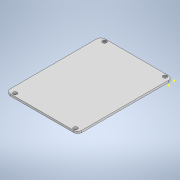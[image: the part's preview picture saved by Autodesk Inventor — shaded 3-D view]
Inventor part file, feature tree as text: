
AUTODESK INVENTOR PART (.ipt)
format: ipt  version: 2022 (Build 260153000, 153)  size: 626,176 bytes
history: native  units: mm
features: extrude x29, sketch x29, projected_geometry x11
ambient origin geometry x8: Origin, YZ Plane, XZ Plane, XY Plane, X Axis, Y Axis, Z Axis, Center Point
bodies: Body1 (feature_tree)
feature tree (69):
  extrude  "Extrusion8"  Depth=3.0mm TaperAngle=0.0deg
  extrude  "Extrusion9"  Depth=71.5mm
  extrude  "Extrusion10"  Depth=8.0mm
  extrude  "Extrusion11"  Depth=8.0mm
  extrude  "Extrusion12"  Depth=6.0mm
  extrude  "Extrusion13"  Depth=8.14mm
  extrude  "Extrusion14"  Depth=7.1mm
  sketch  "Sketch19"  dims[d82=6.0mm d83=7.1mm]
  extrude  "Extrusion16"  Depth=7.0mm
  extrude  "Extrusion17"  Depth=2.5mm
  extrude  "Extrusion18"  Depth=1.0mm
  extrude  "Extrusion19"  Depth=1.5mm
  extrude  "Extrusion20"  Depth=9.0mm TaperAngle=0.0deg
  extrude  "Extrusion21"  Depth=2.0mm
  extrude  "Extrusion24"  Depth=2.0mm
  extrude  "Extrusion25"  Depth=3.0mm TaperAngle=0.0deg
  sketch  "Sketch34"  dims[d117=3.0mm d118=3.0mm]
  extrude  "Extrusion26"  Depth=3.0mm
  extrude  "Extrusion27"  Depth=3.0mm
  extrude  "Extrusion28"  TaperAngle=0.0deg  [1 undecoded]
  extrude  "Extrusion29"  Depth=15.5mm
  extrude  "Extrusion30"  Depth=20.5mm
  extrude  "Extrusion31"  Depth=8.0mm
  extrude  "Extrusion32"  Depth=8.0mm
  extrude  "Extrusion33"  Depth=5.0mm
  extrude  "Extrusion34"  Depth=8.0mm TaperAngle=0.0deg
  extrude  "Extrusion35"  Depth=2.5mm
  extrude  "Extrusion36"  Depth=2.5mm
  extrude  "Extrusion37"  Depth=6.0mm TaperAngle=0.0deg
  extrude  "Extrusion38"  Depth=10.0mm TaperAngle=0.0deg
  extrude  "Extrusion39"  Depth=0.5mm
  sketch  "Sketch12"  dims[d68=3.0mm d69=0.0mm d70=3.0mm d71=0.0mm]
  projected_geometry  "Projected Loop1"
  projected_geometry  "Projected Loop2"
  sketch  "Sketch14"  dims[d72=71.5mm d73=67.15mm]
  sketch  "Sketch15"  dims[d74=8.0mm d75=8.0mm]
  sketch  "Sketch16"  dims[d76=8.0mm d77=8.0mm]
  sketch  "Sketch17"  dims[d78=6.0mm d79=11.8mm]
  sketch  "Sketch18"  dims[d80=6.8mm d81=8.14mm]
  sketch  "Sketch21"  dims[d84=6.0mm d85=7.0mm]
  projected_geometry  "Projected Loop3"
  sketch  "Sketch22"  dims[d86=3.0mm d87=0.0mm d88=2.5mm]
  projected_geometry  "Projected Loop4"
  projected_geometry  "Projected Loop5"
  sketch  "Sketch23"  dims[d89=3.0mm d90=0.0mm d91=1.0mm]
  sketch  "Sketch25"  dims[d92=1.5mm d93=0.0mm d94=5.65mm]
  sketch  "Sketch26"  dims[d95=9.0mm d96=11.17mm d97=0.0mm]
  sketch  "Sketch27"  dims[d98=2.0mm d99=2.0mm]
  sketch  "Sketch32"  dims[d100=2.5mm d101=0.0mm d112=2.0mm]
  sketch  "Sketch33"  dims[d113=2.0mm d114=0.0mm d115=3.0mm d116=0.0mm]
  sketch  "Sketch35"  dims[d119=3.0mm d120=3.0mm]
  sketch  "Sketch37"  dims[d121=0.5mm d122=0.0mm d123=0.0mm]
  sketch  "Sketch38"  dims[d124=0.0mm d125=15.5mm]
  sketch  "Sketch39"  dims[d126=0.0mm d127=20.5mm]
  sketch  "Sketch40"  dims[d128=8.0mm d129=8.0mm]
  projected_geometry  "Projected Loop6"
  sketch  "Sketch41"  dims[d130=8.0mm d131=8.0mm]
  sketch  "Sketch43"  dims[d132=5.3mm d133=5.0mm]
  sketch  "Sketch44"  dims[d134=0.0mm d135=8.0mm d136=0.0mm]
  sketch  "Sketch47"  dims[d137=8.0mm d138=0.0mm d139=2.5mm]
  projected_geometry  "Projected Loop7"
  projected_geometry  "Projected Loop8"
  projected_geometry  "Projected Loop9"
  projected_geometry  "Projected Loop10"
  sketch  "Sketch48"  dims[d140=2.5mm d141=2.5mm]
  projected_geometry  "Projected Loop11"
  sketch  "Sketch49"  dims[d142=2.5mm d143=6.0mm d144=0.0mm]
  sketch  "Sketch50"  dims[d160=100.0mm d161=0.0mm d162=10.0mm d163=0.0mm]
  sketch  "Sketch51"  dims[d164=14.5mm d166=0.74mm d167=100.0mm d168=0.0mm d170=2.5mm d171=2.5mm d172=2.5mm d173=2.5mm d174=5.0mm d175=0.0mm d176=8.0mm d177=8.0mm d178=8.0mm d179=8.0mm d181=53.0mm d182=17.3mm d183=2.0mm d184=2.0mm d185=7.6mm d186=2.1mm d187=2.1mm d190=10.0mm d191=20.0mm d192=3.0mm d193=0.0mm d194=2.5mm d195=2.5mm d196=2.5mm d197=2.5mm d198=5.0mm d199=0.0mm d200=8.0mm d201=8.0mm d202=8.3mm d203=10.0mm d204=10.0mm d205=1.9mm d206=0.0mm d207=10.0mm d208=0.0mm d209=2.5mm d211=2.5mm d212=4.0mm d213=0.0mm d216=22.55489mm d217=8.861037mm d218=2.582mm d219=4.0mm d220=0.0mm d221=8.588357mm d222=5.0mm d223=5.0mm d224=0.0mm d225=10.0mm d226=0.0mm d227=2.85mm d228=14.0mm d229=20.0mm d230=4.0mm d237=68.0mm d239=13.7mm d240=14.9mm d241=4.0mm d242=4.0mm d243=4.0mm d244=4.0mm d245=2.0mm d246=0.0mm d247=1.0mm d248=0.0mm d249=1.0mm d250=0.0mm d251=1.0mm d252=0.0mm d253=8.0mm d254=8.0mm d255=8.0mm d256=8.0mm d257=10.0mm d258=0.0mm d165=0.872665mm d259=0.5mm d260=0.872665mm]
note: 1 required parameter value undecoded (feature->parameter linkage not recoverable at this tier; creation-order binding heuristic only, values carry confidence <= 0.55)
